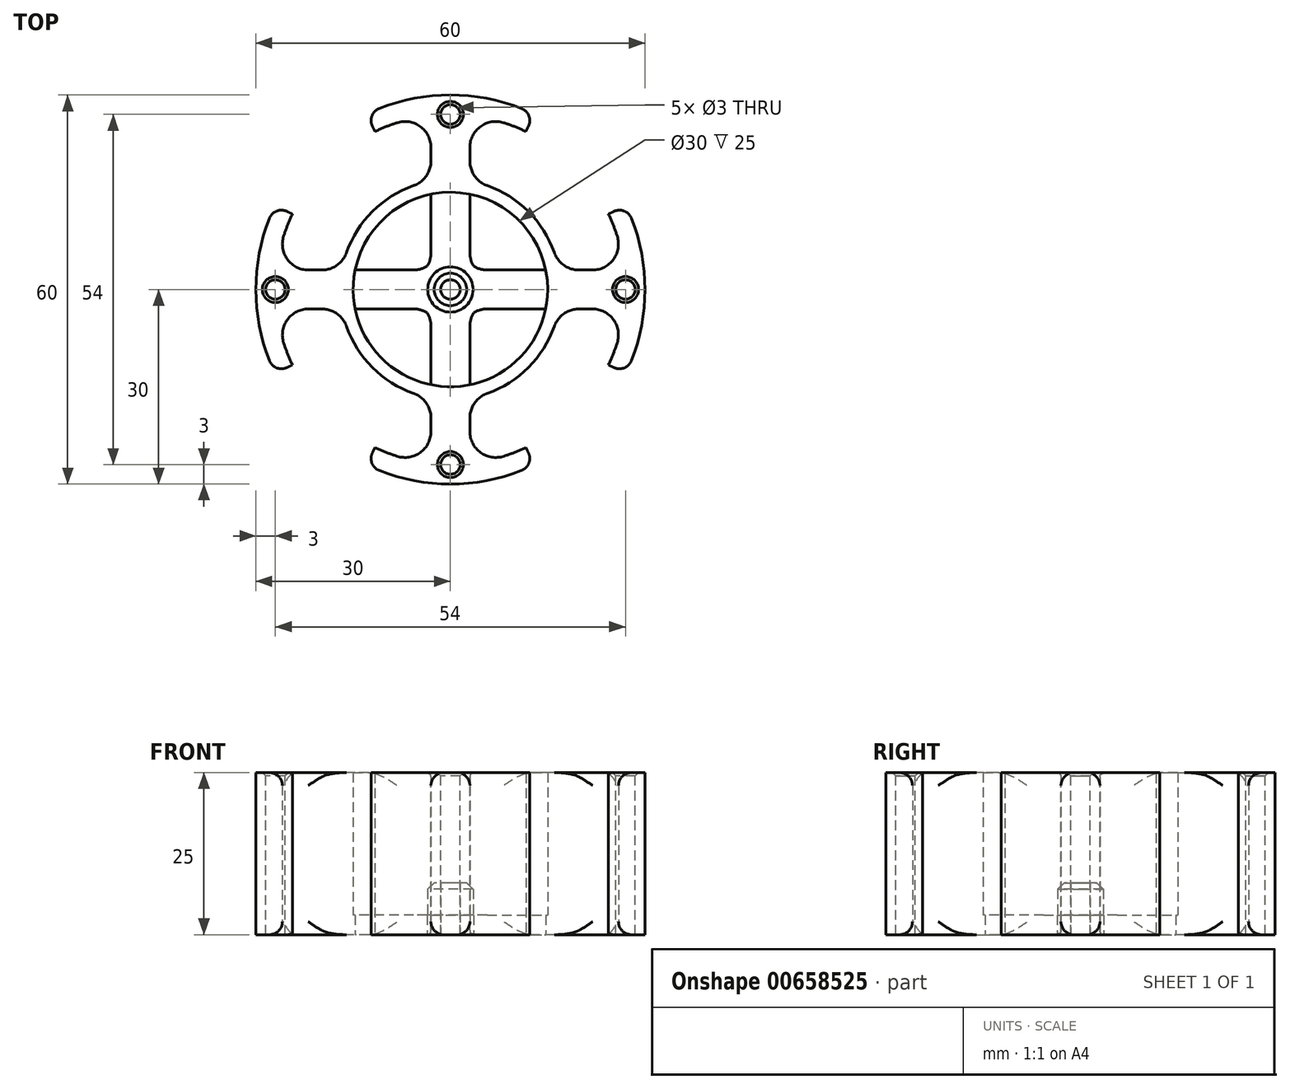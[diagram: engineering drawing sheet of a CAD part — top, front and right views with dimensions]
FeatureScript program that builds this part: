
annotation { "Feature Type Name" : "Feature", "Feature Type Description" : "" }
export const myFeature = defineFeature(function(context is Context, id is Id, definition is map)
    precondition{}
    {
        {
            var Q0;
            Q0=qCreatedBy(makeId("Top.planeOp"),FACE);
            var sketch = newSketch(context, id + "F0", { "sketchPlane" : qUnion([Q0])});
            skCircle(sketch, "E0", {"center": v(0, 0) * mm, "radius": 27 * mm});
            skCircle(sketch, "E1", {"center": v(0, 0) * mm, "radius": 15 * mm});
            skCircle(sketch, "E2", {"center": v(0, 0) * mm, "radius": 17 * mm});
            skCircle(sketch, "E3", {"center": v(0, 0) * mm, "radius": 30 * mm});
            skLineSegment(sketch, "E4", {"start": v(-3, 4) * mm, "end": v(-3, 26.83) * mm});
            skLineSegment(sketch, "E5", {"start": v(3, 4) * mm, "end": v(3, 26.83) * mm});
            skCircle(sketch, "E6", {"center": v(0, 0) * mm, "radius": 5 * mm});
            skLineSegment(sketch, "E7.1.0", {"start": v(4, 3) * mm, "end": v(26.83, 3) * mm});
            skLineSegment(sketch, "E7.1.1", {"start": v(4, -3) * mm, "end": v(26.83, -3) * mm});
            skLineSegment(sketch, "E7.2.0", {"start": v(3, -4) * mm, "end": v(3, -26.83) * mm});
            skLineSegment(sketch, "E7.2.1", {"start": v(-3, -4) * mm, "end": v(-3, -26.83) * mm});
            skLineSegment(sketch, "E7.3.0", {"start": v(-4, -3) * mm, "end": v(-26.83, -3) * mm});
            skLineSegment(sketch, "E7.3.1", {"start": v(-4, 3) * mm, "end": v(-26.83, 3) * mm});
            skLineSegment(sketch, "E7.anchor1", {"start": v(0, 0) * mm, "end": v(-3, 4) * mm, "construction": true});
            skLineSegment(sketch, "E7.anchor2", {"start": v(0, 0) * mm, "end": v(-4, -3) * mm, "construction": true});
            skCircle(sketch, "E8", {"center": v(0, 0) * mm, "radius": 3.5 * mm});
            skCircle(sketch, "E9", {"center": v(0, 0) * mm, "radius": 1.5 * mm});
            skLineSegment(sketch, "E10", {"start": v(-24.36, 11.64) * mm, "end": v(-27.07, 12.93) * mm});
            skLineSegment(sketch, "E11", {"start": v(-11.64, 24.36) * mm, "end": v(-12.93, 27.07) * mm});
            skLineSegment(sketch, "E12", {"start": v(0, 0) * mm, "end": v(-21.21, 21.21) * mm, "construction": true});
            skLineSegment(sketch, "E13.1.0", {"start": v(24.36, 11.64) * mm, "end": v(27.07, 12.93) * mm});
            skLineSegment(sketch, "E13.1.1", {"start": v(11.64, 24.36) * mm, "end": v(12.93, 27.07) * mm});
            skLineSegment(sketch, "E13.2.0", {"start": v(11.64, -24.36) * mm, "end": v(12.93, -27.07) * mm});
            skLineSegment(sketch, "E13.2.1", {"start": v(24.36, -11.64) * mm, "end": v(27.07, -12.93) * mm});
            skLineSegment(sketch, "E13.3.0", {"start": v(-24.36, -11.64) * mm, "end": v(-27.07, -12.93) * mm});
            skLineSegment(sketch, "E13.3.1", {"start": v(-11.64, -24.36) * mm, "end": v(-12.93, -27.07) * mm});
            skLineSegment(sketch, "E13.anchor1", {"start": v(0, 0) * mm, "end": v(-11.64, 24.36) * mm, "construction": true});
            skLineSegment(sketch, "E13.anchor2", {"start": v(0, 0) * mm, "end": v(-24.36, -11.64) * mm, "construction": true});
            skSolve(sketch);
        }
        {
            var Q0;
            Q0=makeQuery(id+"F0.imprint","IMPRINT",FACE,{"disambiguationData":[TD([[makeQuery(id+"F0.imprint","IMPRINT",EDGE,{"derivedFrom":sQuery(id+"F0.wireOp",EDGE,"E8")}),-1.0]])]});
            var Q1;
            {var subQ0=sQuery(id+"F0.wireOp",EDGE,"E7.3.1");var subQ1=sQuery(id+"F0.wireOp",EDGE,"E1");var subQ2=makeQuery(id+"F0.imprint","INTERSECT",VERTEX,{"derivedFrom":[subQ1,subQ0]});Q1=makeQuery(id+"F0.imprint","IMPRINT",FACE,{"disambiguationData":[TD([[makeQuery(id+"F0.imprint","IMPRINT",EDGE,{"disambiguationData":[TD([[subQ2,-1.0]])],"derivedFrom":subQ1}),1.0]])]});}
            var Q2;
            {var subQ0=sQuery(id+"F0.wireOp",EDGE,"E7.1.0");var subQ1=sQuery(id+"F0.wireOp",EDGE,"E1");var subQ2=makeQuery(id+"F0.imprint","INTERSECT",VERTEX,{"derivedFrom":[subQ1,subQ0]});Q2=makeQuery(id+"F0.imprint","IMPRINT",FACE,{"disambiguationData":[TD([[makeQuery(id+"F0.imprint","IMPRINT",EDGE,{"disambiguationData":[TD([[subQ2,1.0]])],"derivedFrom":subQ1}),1.0]])]});}
            var Q3;
            {var subQ0=sQuery(id+"F0.wireOp",EDGE,"E5");var subQ1=sQuery(id+"F0.wireOp",EDGE,"E1");var subQ2=makeQuery(id+"F0.imprint","INTERSECT",VERTEX,{"derivedFrom":[subQ1,subQ0]});Q3=makeQuery(id+"F0.imprint","IMPRINT",FACE,{"disambiguationData":[TD([[makeQuery(id+"F0.imprint","IMPRINT",EDGE,{"disambiguationData":[TD([[subQ2,-1.0]])],"derivedFrom":subQ1}),1.0]])]});}
            var Q4;
            {var subQ0=sQuery(id+"F0.wireOp",EDGE,"E7.2.1");var subQ1=sQuery(id+"F0.wireOp",EDGE,"E1");var subQ2=makeQuery(id+"F0.imprint","INTERSECT",VERTEX,{"derivedFrom":[subQ1,subQ0]});Q4=makeQuery(id+"F0.imprint","IMPRINT",FACE,{"disambiguationData":[TD([[makeQuery(id+"F0.imprint","IMPRINT",EDGE,{"disambiguationData":[TD([[subQ2,-1.0]])],"derivedFrom":subQ1}),1.0]])]});}
            extrude(context, id + "F1", {"entities" : qUnion([Q0, Q1, Q2, Q3, Q4]), "depth" : 3 * mm, "offsetDistance" : 25 * mm});
        }
        {
            var Q0;
            {var subQ0=sQuery(id+"F0.wireOp",EDGE,"E13.1.0");Q0=makeQuery(id+"F0.imprint","IMPRINT",FACE,{"disambiguationData":[TD([[makeQuery(id+"F0.imprint","IMPRINT",EDGE,{"derivedFrom":subQ0}),-1.0]])]});}
            var Q1;
            {var subQ2=sQuery(id+"F0.wireOp",EDGE,"E11");Q1=makeQuery(id+"F0.imprint","IMPRINT",FACE,{"disambiguationData":[TD([[makeQuery(id+"F0.imprint","IMPRINT",EDGE,{"derivedFrom":subQ2}),-1.0]])]});}
            var Q2;
            {var subQ0=sQuery(id+"F0.wireOp",EDGE,"E10");Q2=makeQuery(id+"F0.imprint","IMPRINT",FACE,{"disambiguationData":[TD([[makeQuery(id+"F0.imprint","IMPRINT",EDGE,{"derivedFrom":subQ0}),1.0]])]});}
            var Q3;
            {var subQ0=sQuery(id+"F0.wireOp",EDGE,"E13.2.0");Q3=makeQuery(id+"F0.imprint","IMPRINT",FACE,{"disambiguationData":[TD([[makeQuery(id+"F0.imprint","IMPRINT",EDGE,{"derivedFrom":subQ0}),-1.0]])]});}
            var Q4;
            {var subQ0=sQuery(id+"F0.wireOp",EDGE,"E7.3.0");var subQ1=sQuery(id+"F0.wireOp",EDGE,"E0");var subQ2=makeQuery(id+"F0.imprint","INTERSECT",VERTEX,{"derivedFrom":[subQ1,subQ0]});Q4=makeQuery(id+"F0.imprint","IMPRINT",FACE,{"disambiguationData":[TD([[makeQuery(id+"F0.imprint","IMPRINT",EDGE,{"disambiguationData":[TD([[subQ2,1.0]])],"derivedFrom":subQ1}),1.0]])]});}
            var Q5;
            {var subQ0=sQuery(id+"F0.wireOp",EDGE,"E7.3.1");var subQ1=sQuery(id+"F0.wireOp",EDGE,"E1");var subQ2=makeQuery(id+"F0.imprint","INTERSECT",VERTEX,{"derivedFrom":[subQ1,subQ0]});Q5=makeQuery(id+"F0.imprint","IMPRINT",FACE,{"disambiguationData":[TD([[makeQuery(id+"F0.imprint","IMPRINT",EDGE,{"disambiguationData":[TD([[subQ2,-1.0]])],"derivedFrom":subQ1}),-1.0]])]});}
            var Q6;
            {var subQ0=sQuery(id+"F0.wireOp",EDGE,"E7.1.0");var subQ1=sQuery(id+"F0.wireOp",EDGE,"E1");var subQ2=makeQuery(id+"F0.imprint","INTERSECT",VERTEX,{"derivedFrom":[subQ1,subQ0]});Q6=makeQuery(id+"F0.imprint","IMPRINT",FACE,{"disambiguationData":[TD([[makeQuery(id+"F0.imprint","IMPRINT",EDGE,{"disambiguationData":[TD([[subQ2,1.0]])],"derivedFrom":subQ1}),-1.0]])]});}
            var Q7;
            {var subQ0=sQuery(id+"F0.wireOp",EDGE,"E7.1.0");var subQ1=sQuery(id+"F0.wireOp",EDGE,"E0");var subQ2=makeQuery(id+"F0.imprint","INTERSECT",VERTEX,{"derivedFrom":[subQ1,subQ0]});Q7=makeQuery(id+"F0.imprint","IMPRINT",FACE,{"disambiguationData":[TD([[makeQuery(id+"F0.imprint","IMPRINT",EDGE,{"disambiguationData":[TD([[subQ2,1.0]])],"derivedFrom":subQ1}),1.0]])]});}
            var Q8;
            {var subQ0=sQuery(id+"F0.wireOp",EDGE,"E5");var subQ1=sQuery(id+"F0.wireOp",EDGE,"E1");var subQ2=makeQuery(id+"F0.imprint","INTERSECT",VERTEX,{"derivedFrom":[subQ1,subQ0]});Q8=makeQuery(id+"F0.imprint","IMPRINT",FACE,{"disambiguationData":[TD([[makeQuery(id+"F0.imprint","IMPRINT",EDGE,{"disambiguationData":[TD([[subQ2,-1.0]])],"derivedFrom":subQ1}),-1.0]])]});}
            var Q9;
            {var subQ0=sQuery(id+"F0.wireOp",EDGE,"E4");var subQ1=sQuery(id+"F0.wireOp",EDGE,"E0");var subQ2=makeQuery(id+"F0.imprint","INTERSECT",VERTEX,{"derivedFrom":[subQ1,subQ0]});Q9=makeQuery(id+"F0.imprint","IMPRINT",FACE,{"disambiguationData":[TD([[makeQuery(id+"F0.imprint","IMPRINT",EDGE,{"disambiguationData":[TD([[subQ2,1.0]])],"derivedFrom":subQ1}),1.0]])]});}
            var Q10;
            {var subQ0=sQuery(id+"F0.wireOp",EDGE,"E5");var subQ1=sQuery(id+"F0.wireOp",EDGE,"E1");var subQ2=makeQuery(id+"F0.imprint","INTERSECT",VERTEX,{"derivedFrom":[subQ1,subQ0]});Q10=makeQuery(id+"F0.imprint","IMPRINT",FACE,{"disambiguationData":[TD([[makeQuery(id+"F0.imprint","IMPRINT",EDGE,{"disambiguationData":[TD([[subQ2,1.0]])],"derivedFrom":subQ1}),-1.0]])]});}
            var Q11;
            {var subQ0=sQuery(id+"F0.wireOp",EDGE,"E4");var subQ1=sQuery(id+"F0.wireOp",EDGE,"E1");var subQ2=makeQuery(id+"F0.imprint","INTERSECT",VERTEX,{"derivedFrom":[subQ1,subQ0]});Q11=makeQuery(id+"F0.imprint","IMPRINT",FACE,{"disambiguationData":[TD([[makeQuery(id+"F0.imprint","IMPRINT",EDGE,{"disambiguationData":[TD([[subQ2,-1.0]])],"derivedFrom":subQ1}),-1.0]])]});}
            var Q12;
            {var subQ0=sQuery(id+"F0.wireOp",EDGE,"E7.2.0");var subQ1=sQuery(id+"F0.wireOp",EDGE,"E0");var subQ2=makeQuery(id+"F0.imprint","INTERSECT",VERTEX,{"derivedFrom":[subQ1,subQ0]});Q12=makeQuery(id+"F0.imprint","IMPRINT",FACE,{"disambiguationData":[TD([[makeQuery(id+"F0.imprint","IMPRINT",EDGE,{"disambiguationData":[TD([[subQ2,1.0]])],"derivedFrom":subQ1}),1.0]])]});}
            var Q13;
            {var subQ0=sQuery(id+"F0.wireOp",EDGE,"E7.2.1");var subQ1=sQuery(id+"F0.wireOp",EDGE,"E1");var subQ2=makeQuery(id+"F0.imprint","INTERSECT",VERTEX,{"derivedFrom":[subQ1,subQ0]});Q13=makeQuery(id+"F0.imprint","IMPRINT",FACE,{"disambiguationData":[TD([[makeQuery(id+"F0.imprint","IMPRINT",EDGE,{"disambiguationData":[TD([[subQ2,-1.0]])],"derivedFrom":subQ1}),-1.0]])]});}
            var Q14;
            {var subQ0=sQuery(id+"F0.wireOp",EDGE,"E7.3.0");var subQ1=sQuery(id+"F0.wireOp",EDGE,"E1");var subQ2=makeQuery(id+"F0.imprint","INTERSECT",VERTEX,{"derivedFrom":[subQ1,subQ0]});Q14=makeQuery(id+"F0.imprint","IMPRINT",FACE,{"disambiguationData":[TD([[makeQuery(id+"F0.imprint","IMPRINT",EDGE,{"disambiguationData":[TD([[subQ2,-1.0]])],"derivedFrom":subQ1}),-1.0]])]});}
            var Q15;
            {var subQ0=sQuery(id+"F0.wireOp",EDGE,"E7.2.0");var subQ1=sQuery(id+"F0.wireOp",EDGE,"E1");var subQ2=makeQuery(id+"F0.imprint","INTERSECT",VERTEX,{"derivedFrom":[subQ1,subQ0]});Q15=makeQuery(id+"F0.imprint","IMPRINT",FACE,{"disambiguationData":[TD([[makeQuery(id+"F0.imprint","IMPRINT",EDGE,{"disambiguationData":[TD([[subQ2,-1.0]])],"derivedFrom":subQ1}),-1.0]])]});}
            extrude(context, id + "F2", {"entities" : qUnion([Q0, Q1, Q2, Q3, Q4, Q5, Q6, Q7, Q8, Q9, Q10, Q11, Q12, Q13, Q14, Q15]), "operationType" : NewBodyOperationType.ADD, "depth" : 25 * mm, "offsetDistance" : 25 * mm});
        }
        {
            var Q0;
            Q0=makeQuery(id+"F0.imprint","IMPRINT",FACE,{"disambiguationData":[TD([[makeQuery(id+"F0.imprint","IMPRINT",EDGE,{"derivedFrom":sQuery(id+"F0.wireOp",EDGE,"E8")}),1.0]])]});
            extrude(context, id + "F3", {"entities" : qUnion([Q0]), "operationType" : NewBodyOperationType.ADD, "depth" : 8 * mm, "offsetDistance" : 25 * mm});
        }
        {
            var Q0;
            Q0=makeQuery(id+"F3.opExtrude","CAP_EDGE",EDGE,{"disambiguationData":[OSD([sQuery(id+"F0.wireOp",EDGE,"E8")])],"isStart":false});
            chamfer(context, id + "F4", {"entities" : qUnion([Q0]), "width" : 1 * mm, "tangentPropagation" : true});
        }
        {
            var Q0;
            Q0=makeQuery(id+"F2.opExtrude","SWEPT_EDGE",EDGE,{"disambiguationData":[OSD([sQuery(id+"F0.wireOp",EDGE,"E0"),sQuery(id+"F0.wireOp",EDGE,"E7.1.0")])]});
            var Q1;
            Q1=makeQuery(id+"F2.opExtrude","SWEPT_EDGE",EDGE,{"disambiguationData":[OSD([sQuery(id+"F0.wireOp",EDGE,"E2"),sQuery(id+"F0.wireOp",EDGE,"E7.1.0")])]});
            var Q2;
            Q2=makeQuery(id+"F2.opExtrude","SWEPT_EDGE",EDGE,{"disambiguationData":[OSD([sQuery(id+"F0.wireOp",EDGE,"E2"),sQuery(id+"F0.wireOp",EDGE,"E5")])]});
            var Q3;
            Q3=makeQuery(id+"F2.opExtrude","SWEPT_EDGE",EDGE,{"disambiguationData":[OSD([sQuery(id+"F0.wireOp",EDGE,"E0"),sQuery(id+"F0.wireOp",EDGE,"E5")])]});
            var Q4;
            Q4=makeQuery(id+"F2.opExtrude","SWEPT_EDGE",EDGE,{"disambiguationData":[OSD([sQuery(id+"F0.wireOp",EDGE,"E2"),sQuery(id+"F0.wireOp",EDGE,"E4")])]});
            var Q5;
            Q5=makeQuery(id+"F2.opExtrude","SWEPT_EDGE",EDGE,{"disambiguationData":[OSD([sQuery(id+"F0.wireOp",EDGE,"E0"),sQuery(id+"F0.wireOp",EDGE,"E4")])]});
            var Q6;
            Q6=makeQuery(id+"F2.opExtrude","SWEPT_EDGE",EDGE,{"disambiguationData":[OSD([sQuery(id+"F0.wireOp",EDGE,"E2"),sQuery(id+"F0.wireOp",EDGE,"E7.3.1")])]});
            var Q7;
            Q7=makeQuery(id+"F2.opExtrude","SWEPT_EDGE",EDGE,{"disambiguationData":[OSD([sQuery(id+"F0.wireOp",EDGE,"E0"),sQuery(id+"F0.wireOp",EDGE,"E7.3.1")])]});
            var Q8;
            Q8=makeQuery(id+"F2.opExtrude","SWEPT_EDGE",EDGE,{"disambiguationData":[OSD([sQuery(id+"F0.wireOp",EDGE,"E0"),sQuery(id+"F0.wireOp",EDGE,"E7.2.0")])]});
            var Q9;
            Q9=makeQuery(id+"F2.opExtrude","SWEPT_EDGE",EDGE,{"disambiguationData":[OSD([sQuery(id+"F0.wireOp",EDGE,"E2"),sQuery(id+"F0.wireOp",EDGE,"E7.2.0")])]});
            var Q10;
            Q10=makeQuery(id+"F2.opExtrude","SWEPT_EDGE",EDGE,{"disambiguationData":[OSD([sQuery(id+"F0.wireOp",EDGE,"E2"),sQuery(id+"F0.wireOp",EDGE,"E7.1.1")])]});
            var Q11;
            Q11=makeQuery(id+"F2.opExtrude","SWEPT_EDGE",EDGE,{"disambiguationData":[OSD([sQuery(id+"F0.wireOp",EDGE,"E0"),sQuery(id+"F0.wireOp",EDGE,"E7.1.1")])]});
            var Q12;
            Q12=makeQuery(id+"F2.opExtrude","SWEPT_EDGE",EDGE,{"disambiguationData":[OSD([sQuery(id+"F0.wireOp",EDGE,"E0"),sQuery(id+"F0.wireOp",EDGE,"E7.3.0")])]});
            var Q13;
            Q13=makeQuery(id+"F2.opExtrude","SWEPT_EDGE",EDGE,{"disambiguationData":[OSD([sQuery(id+"F0.wireOp",EDGE,"E2"),sQuery(id+"F0.wireOp",EDGE,"E7.3.0")])]});
            var Q14;
            Q14=makeQuery(id+"F2.opExtrude","SWEPT_EDGE",EDGE,{"disambiguationData":[OSD([sQuery(id+"F0.wireOp",EDGE,"E2"),sQuery(id+"F0.wireOp",EDGE,"E7.2.1")])]});
            var Q15;
            Q15=makeQuery(id+"F2.opExtrude","SWEPT_EDGE",EDGE,{"disambiguationData":[OSD([sQuery(id+"F0.wireOp",EDGE,"E0"),sQuery(id+"F0.wireOp",EDGE,"E7.2.1")])]});
            var Q16;
            Q16=makeQuery(id+"F1.opExtrude","SWEPT_EDGE",EDGE,{"disambiguationData":[OSD([sQuery(id+"F0.wireOp",EDGE,"E1"),sQuery(id+"F0.wireOp",EDGE,"E7.3.0")])]});
            var Q17;
            Q17=makeQuery(id+"F1.opExtrude","SWEPT_EDGE",EDGE,{"disambiguationData":[OSD([sQuery(id+"F0.wireOp",EDGE,"E1"),sQuery(id+"F0.wireOp",EDGE,"E7.2.1")])]});
            var Q18;
            Q18=makeQuery(id+"F1.opExtrude","SWEPT_EDGE",EDGE,{"disambiguationData":[OSD([sQuery(id+"F0.wireOp",EDGE,"E1"),sQuery(id+"F0.wireOp",EDGE,"E7.2.0")])]});
            var Q19;
            Q19=makeQuery(id+"F1.opExtrude","SWEPT_EDGE",EDGE,{"disambiguationData":[OSD([sQuery(id+"F0.wireOp",EDGE,"E1"),sQuery(id+"F0.wireOp",EDGE,"E7.1.1")])]});
            var Q20;
            Q20=makeQuery(id+"F1.opExtrude","SWEPT_EDGE",EDGE,{"disambiguationData":[OSD([sQuery(id+"F0.wireOp",EDGE,"E1"),sQuery(id+"F0.wireOp",EDGE,"E4")])]});
            var Q21;
            Q21=makeQuery(id+"F1.opExtrude","SWEPT_EDGE",EDGE,{"disambiguationData":[OSD([sQuery(id+"F0.wireOp",EDGE,"E1"),sQuery(id+"F0.wireOp",EDGE,"E7.1.0")])]});
            var Q22;
            Q22=makeQuery(id+"F1.opExtrude","SWEPT_EDGE",EDGE,{"disambiguationData":[OSD([sQuery(id+"F0.wireOp",EDGE,"E1"),sQuery(id+"F0.wireOp",EDGE,"E5")])]});
            var Q23;
            Q23=makeQuery(id+"F1.opExtrude","SWEPT_EDGE",EDGE,{"disambiguationData":[OSD([sQuery(id+"F0.wireOp",EDGE,"E1"),sQuery(id+"F0.wireOp",EDGE,"E7.3.1")])]});
            var Q24;
            Q24=makeQuery(id+"F1.opExtrude","SWEPT_EDGE",EDGE,{"disambiguationData":[OSD([sQuery(id+"F0.wireOp",EDGE,"E4"),sQuery(id+"F0.wireOp",EDGE,"E6")])]});
            var Q25;
            Q25=makeQuery(id+"F1.opExtrude","SWEPT_EDGE",EDGE,{"disambiguationData":[OSD([sQuery(id+"F0.wireOp",EDGE,"E6"),sQuery(id+"F0.wireOp",EDGE,"E7.3.1")])]});
            var Q26;
            Q26=makeQuery(id+"F1.opExtrude","SWEPT_EDGE",EDGE,{"disambiguationData":[OSD([sQuery(id+"F0.wireOp",EDGE,"E6"),sQuery(id+"F0.wireOp",EDGE,"E7.3.0")])]});
            var Q27;
            Q27=makeQuery(id+"F1.opExtrude","SWEPT_EDGE",EDGE,{"disambiguationData":[OSD([sQuery(id+"F0.wireOp",EDGE,"E6"),sQuery(id+"F0.wireOp",EDGE,"E7.2.1")])]});
            var Q28;
            Q28=makeQuery(id+"F1.opExtrude","SWEPT_EDGE",EDGE,{"disambiguationData":[OSD([sQuery(id+"F0.wireOp",EDGE,"E6"),sQuery(id+"F0.wireOp",EDGE,"E7.2.0")])]});
            var Q29;
            Q29=makeQuery(id+"F1.opExtrude","SWEPT_EDGE",EDGE,{"disambiguationData":[OSD([sQuery(id+"F0.wireOp",EDGE,"E6"),sQuery(id+"F0.wireOp",EDGE,"E7.1.1")])]});
            var Q30;
            Q30=makeQuery(id+"F1.opExtrude","SWEPT_EDGE",EDGE,{"disambiguationData":[OSD([sQuery(id+"F0.wireOp",EDGE,"E5"),sQuery(id+"F0.wireOp",EDGE,"E6")])]});
            var Q31;
            Q31=makeQuery(id+"F1.opExtrude","SWEPT_EDGE",EDGE,{"disambiguationData":[OSD([sQuery(id+"F0.wireOp",EDGE,"E6"),sQuery(id+"F0.wireOp",EDGE,"E7.1.0")])]});
            fillet(context, id + "F5", {"entities" : qUnion([Q0, Q1, Q2, Q3, Q4, Q5, Q6, Q7, Q8, Q9, Q10, Q11, Q12, Q13, Q14, Q15, Q16, Q17, Q18, Q19, Q20, Q21, Q22, Q23, Q24, Q25, Q26, Q27, Q28, Q29, Q30, Q31]), "radius" : 4 * mm, "tangentPropagation" : true, "allowEdgeOverflow" : false});
        }
        {
            var Q0;
            Q0=makeQuery(id+"F2.opExtrude","CAP_FACE",FACE,{"disambiguationData":[OSD([sQuery(id+"F0.wireOp",EDGE,"E0"),sQuery(id+"F0.wireOp",EDGE,"E1"),sQuery(id+"F0.wireOp",EDGE,"E2"),sQuery(id+"F0.wireOp",EDGE,"E3"),sQuery(id+"F0.wireOp",EDGE,"E4"),sQuery(id+"F0.wireOp",EDGE,"E5"),sQuery(id+"F0.wireOp",EDGE,"E7.1.0"),sQuery(id+"F0.wireOp",EDGE,"E7.1.1"),sQuery(id+"F0.wireOp",EDGE,"E7.2.0"),sQuery(id+"F0.wireOp",EDGE,"E7.2.1"),sQuery(id+"F0.wireOp",EDGE,"E7.3.0"),sQuery(id+"F0.wireOp",EDGE,"E7.3.1")])],"isStart":false});
            var sketch = newSketch(context, id + "F6", { "sketchPlane" : qUnion([Q0])});
            skCircle(sketch, "E14.0", {"center": v(0, 0) * mm, "radius": 27 * mm});
            skPoint(sketch, "E15", {"position": v(0, 27) * mm});
            skPoint(sketch, "E16", {"position": v(27, 0) * mm});
            skPoint(sketch, "E17", {"position": v(-27, 0) * mm});
            skPoint(sketch, "E18", {"position": v(0, -27) * mm});
            skSolve(sketch);
        }
        {
            var Q0;
            Q0=sQuery(id+"F6.wireOp",VERTEX,"E15");
            var Q1;
            Q1=sQuery(id+"F6.wireOp",VERTEX,"E16");
            var Q2;
            Q2=sQuery(id+"F6.wireOp",VERTEX,"E18");
            var Q3;
            Q3=sQuery(id+"F6.wireOp",VERTEX,"E17");
            var Q4;
            Q4=makeQuery(id+"F1.opExtrude","SWEPT_BODY",BODY,{"disambiguationData":[OSD([sQuery(id+"F0.wireOp",EDGE,"E1"),sQuery(id+"F0.wireOp",EDGE,"E4"),sQuery(id+"F0.wireOp",EDGE,"E5"),sQuery(id+"F0.wireOp",EDGE,"E6"),sQuery(id+"F0.wireOp",EDGE,"E7.1.0"),sQuery(id+"F0.wireOp",EDGE,"E7.1.1"),sQuery(id+"F0.wireOp",EDGE,"E7.2.0"),sQuery(id+"F0.wireOp",EDGE,"E7.2.1"),sQuery(id+"F0.wireOp",EDGE,"E7.3.0"),sQuery(id+"F0.wireOp",EDGE,"E7.3.1"),sQuery(id+"F0.wireOp",EDGE,"E8")])]});
            hole(context, id + "F7", {"style" : HoleStyle.C_SINK, "endStyle" : HoleEndStyle.THROUGH, "holeDiameter" : 3 * mm, "cSinkDiameter" : 4 * mm, "cSinkAngle" : 90 * degree, "majorDiameter" : 5 * mm, "isTappedThrough" : true, "tappedDepth" : 12 * mm, "tapClearance" : 3, "startFromSketch" : true, "locations" : qUnion([Q0, Q1, Q2, Q3]), "scope" : qUnion([Q4])});
        }
        {
            var Q0;
            {var subQ0=sQuery(id+"F0.wireOp",EDGE,"E7.3.0");var subQ1=sQuery(id+"F0.wireOp",EDGE,"E0");Q0=makeQuery(id+"F5.opFillet","BLEND_EDGE",EDGE,{"blendedFrom":[makeQuery(id+"F2.opExtrude","SWEPT_EDGE",EDGE,{"disambiguationData":[OSD([subQ1,subQ0])]}),makeQuery(id+"F2.opExtrude","CAP_FACE",FACE,{"disambiguationData":[OSD([subQ1,sQuery(id+"F0.wireOp",EDGE,"E1"),sQuery(id+"F0.wireOp",EDGE,"E2"),sQuery(id+"F0.wireOp",EDGE,"E3"),sQuery(id+"F0.wireOp",EDGE,"E4"),sQuery(id+"F0.wireOp",EDGE,"E5"),sQuery(id+"F0.wireOp",EDGE,"E7.1.0"),sQuery(id+"F0.wireOp",EDGE,"E7.1.1"),sQuery(id+"F0.wireOp",EDGE,"E7.2.0"),sQuery(id+"F0.wireOp",EDGE,"E7.2.1"),subQ0,sQuery(id+"F0.wireOp",EDGE,"E7.3.1"),sQuery(id+"F0.wireOp",EDGE,"E10"),sQuery(id+"F0.wireOp",EDGE,"E11"),sQuery(id+"F0.wireOp",EDGE,"E13.1.0"),sQuery(id+"F0.wireOp",EDGE,"E13.1.1"),sQuery(id+"F0.wireOp",EDGE,"E13.2.0"),sQuery(id+"F0.wireOp",EDGE,"E13.2.1"),sQuery(id+"F0.wireOp",EDGE,"E13.3.0"),sQuery(id+"F0.wireOp",EDGE,"E13.3.1")])],"isStart":false})],"blendedInto":[makeQuery(id+"F2.opExtrude","CAP_FACE",FACE,{"disambiguationData":[OSD([subQ1,sQuery(id+"F0.wireOp",EDGE,"E1"),sQuery(id+"F0.wireOp",EDGE,"E2"),sQuery(id+"F0.wireOp",EDGE,"E3"),sQuery(id+"F0.wireOp",EDGE,"E4"),sQuery(id+"F0.wireOp",EDGE,"E5"),sQuery(id+"F0.wireOp",EDGE,"E7.1.0"),sQuery(id+"F0.wireOp",EDGE,"E7.1.1"),sQuery(id+"F0.wireOp",EDGE,"E7.2.0"),sQuery(id+"F0.wireOp",EDGE,"E7.2.1"),subQ0,sQuery(id+"F0.wireOp",EDGE,"E7.3.1"),sQuery(id+"F0.wireOp",EDGE,"E10"),sQuery(id+"F0.wireOp",EDGE,"E11"),sQuery(id+"F0.wireOp",EDGE,"E13.1.0"),sQuery(id+"F0.wireOp",EDGE,"E13.1.1"),sQuery(id+"F0.wireOp",EDGE,"E13.2.0"),sQuery(id+"F0.wireOp",EDGE,"E13.2.1"),sQuery(id+"F0.wireOp",EDGE,"E13.3.0"),sQuery(id+"F0.wireOp",EDGE,"E13.3.1")])],"isStart":false})]});}
            var Q1;
            {var subQ0=sQuery(id+"F0.wireOp",EDGE,"E7.3.1");var subQ1=sQuery(id+"F0.wireOp",EDGE,"E0");Q1=makeQuery(id+"F5.opFillet","BLEND_EDGE",EDGE,{"blendedFrom":[makeQuery(id+"F2.opExtrude","SWEPT_EDGE",EDGE,{"disambiguationData":[OSD([subQ1,subQ0])]}),makeQuery(id+"F2.opExtrude","CAP_FACE",FACE,{"disambiguationData":[OSD([subQ1,sQuery(id+"F0.wireOp",EDGE,"E1"),sQuery(id+"F0.wireOp",EDGE,"E2"),sQuery(id+"F0.wireOp",EDGE,"E3"),sQuery(id+"F0.wireOp",EDGE,"E4"),sQuery(id+"F0.wireOp",EDGE,"E5"),sQuery(id+"F0.wireOp",EDGE,"E7.1.0"),sQuery(id+"F0.wireOp",EDGE,"E7.1.1"),sQuery(id+"F0.wireOp",EDGE,"E7.2.0"),sQuery(id+"F0.wireOp",EDGE,"E7.2.1"),sQuery(id+"F0.wireOp",EDGE,"E7.3.0"),subQ0,sQuery(id+"F0.wireOp",EDGE,"E10"),sQuery(id+"F0.wireOp",EDGE,"E11"),sQuery(id+"F0.wireOp",EDGE,"E13.1.0"),sQuery(id+"F0.wireOp",EDGE,"E13.1.1"),sQuery(id+"F0.wireOp",EDGE,"E13.2.0"),sQuery(id+"F0.wireOp",EDGE,"E13.2.1"),sQuery(id+"F0.wireOp",EDGE,"E13.3.0"),sQuery(id+"F0.wireOp",EDGE,"E13.3.1")])],"isStart":false})],"blendedInto":[makeQuery(id+"F2.opExtrude","CAP_FACE",FACE,{"disambiguationData":[OSD([subQ1,sQuery(id+"F0.wireOp",EDGE,"E1"),sQuery(id+"F0.wireOp",EDGE,"E2"),sQuery(id+"F0.wireOp",EDGE,"E3"),sQuery(id+"F0.wireOp",EDGE,"E4"),sQuery(id+"F0.wireOp",EDGE,"E5"),sQuery(id+"F0.wireOp",EDGE,"E7.1.0"),sQuery(id+"F0.wireOp",EDGE,"E7.1.1"),sQuery(id+"F0.wireOp",EDGE,"E7.2.0"),sQuery(id+"F0.wireOp",EDGE,"E7.2.1"),sQuery(id+"F0.wireOp",EDGE,"E7.3.0"),subQ0,sQuery(id+"F0.wireOp",EDGE,"E10"),sQuery(id+"F0.wireOp",EDGE,"E11"),sQuery(id+"F0.wireOp",EDGE,"E13.1.0"),sQuery(id+"F0.wireOp",EDGE,"E13.1.1"),sQuery(id+"F0.wireOp",EDGE,"E13.2.0"),sQuery(id+"F0.wireOp",EDGE,"E13.2.1"),sQuery(id+"F0.wireOp",EDGE,"E13.3.0"),sQuery(id+"F0.wireOp",EDGE,"E13.3.1")])],"isStart":false})]});}
            var Q2;
            {var subQ0=sQuery(id+"F0.wireOp",EDGE,"E4");var subQ1=sQuery(id+"F0.wireOp",EDGE,"E0");Q2=makeQuery(id+"F5.opFillet","BLEND_EDGE",EDGE,{"blendedFrom":[makeQuery(id+"F2.opExtrude","SWEPT_EDGE",EDGE,{"disambiguationData":[OSD([subQ1,subQ0])]}),makeQuery(id+"F2.opExtrude","CAP_FACE",FACE,{"disambiguationData":[OSD([subQ1,sQuery(id+"F0.wireOp",EDGE,"E1"),sQuery(id+"F0.wireOp",EDGE,"E2"),sQuery(id+"F0.wireOp",EDGE,"E3"),subQ0,sQuery(id+"F0.wireOp",EDGE,"E5"),sQuery(id+"F0.wireOp",EDGE,"E7.1.0"),sQuery(id+"F0.wireOp",EDGE,"E7.1.1"),sQuery(id+"F0.wireOp",EDGE,"E7.2.0"),sQuery(id+"F0.wireOp",EDGE,"E7.2.1"),sQuery(id+"F0.wireOp",EDGE,"E7.3.0"),sQuery(id+"F0.wireOp",EDGE,"E7.3.1"),sQuery(id+"F0.wireOp",EDGE,"E10"),sQuery(id+"F0.wireOp",EDGE,"E11"),sQuery(id+"F0.wireOp",EDGE,"E13.1.0"),sQuery(id+"F0.wireOp",EDGE,"E13.1.1"),sQuery(id+"F0.wireOp",EDGE,"E13.2.0"),sQuery(id+"F0.wireOp",EDGE,"E13.2.1"),sQuery(id+"F0.wireOp",EDGE,"E13.3.0"),sQuery(id+"F0.wireOp",EDGE,"E13.3.1")])],"isStart":false})],"blendedInto":[makeQuery(id+"F2.opExtrude","CAP_FACE",FACE,{"disambiguationData":[OSD([subQ1,sQuery(id+"F0.wireOp",EDGE,"E1"),sQuery(id+"F0.wireOp",EDGE,"E2"),sQuery(id+"F0.wireOp",EDGE,"E3"),subQ0,sQuery(id+"F0.wireOp",EDGE,"E5"),sQuery(id+"F0.wireOp",EDGE,"E7.1.0"),sQuery(id+"F0.wireOp",EDGE,"E7.1.1"),sQuery(id+"F0.wireOp",EDGE,"E7.2.0"),sQuery(id+"F0.wireOp",EDGE,"E7.2.1"),sQuery(id+"F0.wireOp",EDGE,"E7.3.0"),sQuery(id+"F0.wireOp",EDGE,"E7.3.1"),sQuery(id+"F0.wireOp",EDGE,"E10"),sQuery(id+"F0.wireOp",EDGE,"E11"),sQuery(id+"F0.wireOp",EDGE,"E13.1.0"),sQuery(id+"F0.wireOp",EDGE,"E13.1.1"),sQuery(id+"F0.wireOp",EDGE,"E13.2.0"),sQuery(id+"F0.wireOp",EDGE,"E13.2.1"),sQuery(id+"F0.wireOp",EDGE,"E13.3.0"),sQuery(id+"F0.wireOp",EDGE,"E13.3.1")])],"isStart":false})]});}
            var Q3;
            {var subQ0=sQuery(id+"F0.wireOp",EDGE,"E7.2.1");var subQ1=sQuery(id+"F0.wireOp",EDGE,"E0");Q3=makeQuery(id+"F5.opFillet","BLEND_EDGE",EDGE,{"blendedFrom":[makeQuery(id+"F2.opExtrude","SWEPT_EDGE",EDGE,{"disambiguationData":[OSD([subQ1,subQ0])]}),makeQuery(id+"F2.opExtrude","CAP_FACE",FACE,{"disambiguationData":[OSD([subQ1,sQuery(id+"F0.wireOp",EDGE,"E1"),sQuery(id+"F0.wireOp",EDGE,"E2"),sQuery(id+"F0.wireOp",EDGE,"E3"),sQuery(id+"F0.wireOp",EDGE,"E4"),sQuery(id+"F0.wireOp",EDGE,"E5"),sQuery(id+"F0.wireOp",EDGE,"E7.1.0"),sQuery(id+"F0.wireOp",EDGE,"E7.1.1"),sQuery(id+"F0.wireOp",EDGE,"E7.2.0"),subQ0,sQuery(id+"F0.wireOp",EDGE,"E7.3.0"),sQuery(id+"F0.wireOp",EDGE,"E7.3.1"),sQuery(id+"F0.wireOp",EDGE,"E10"),sQuery(id+"F0.wireOp",EDGE,"E11"),sQuery(id+"F0.wireOp",EDGE,"E13.1.0"),sQuery(id+"F0.wireOp",EDGE,"E13.1.1"),sQuery(id+"F0.wireOp",EDGE,"E13.2.0"),sQuery(id+"F0.wireOp",EDGE,"E13.2.1"),sQuery(id+"F0.wireOp",EDGE,"E13.3.0"),sQuery(id+"F0.wireOp",EDGE,"E13.3.1")])],"isStart":false})],"blendedInto":[makeQuery(id+"F2.opExtrude","CAP_FACE",FACE,{"disambiguationData":[OSD([subQ1,sQuery(id+"F0.wireOp",EDGE,"E1"),sQuery(id+"F0.wireOp",EDGE,"E2"),sQuery(id+"F0.wireOp",EDGE,"E3"),sQuery(id+"F0.wireOp",EDGE,"E4"),sQuery(id+"F0.wireOp",EDGE,"E5"),sQuery(id+"F0.wireOp",EDGE,"E7.1.0"),sQuery(id+"F0.wireOp",EDGE,"E7.1.1"),sQuery(id+"F0.wireOp",EDGE,"E7.2.0"),subQ0,sQuery(id+"F0.wireOp",EDGE,"E7.3.0"),sQuery(id+"F0.wireOp",EDGE,"E7.3.1"),sQuery(id+"F0.wireOp",EDGE,"E10"),sQuery(id+"F0.wireOp",EDGE,"E11"),sQuery(id+"F0.wireOp",EDGE,"E13.1.0"),sQuery(id+"F0.wireOp",EDGE,"E13.1.1"),sQuery(id+"F0.wireOp",EDGE,"E13.2.0"),sQuery(id+"F0.wireOp",EDGE,"E13.2.1"),sQuery(id+"F0.wireOp",EDGE,"E13.3.0"),sQuery(id+"F0.wireOp",EDGE,"E13.3.1")])],"isStart":false})]});}
            var Q4;
            {var subQ0=sQuery(id+"F0.wireOp",EDGE,"E7.2.0");var subQ1=sQuery(id+"F0.wireOp",EDGE,"E0");Q4=makeQuery(id+"F5.opFillet","BLEND_EDGE",EDGE,{"blendedFrom":[makeQuery(id+"F2.opExtrude","SWEPT_EDGE",EDGE,{"disambiguationData":[OSD([subQ1,subQ0])]}),makeQuery(id+"F2.opExtrude","CAP_FACE",FACE,{"disambiguationData":[OSD([subQ1,sQuery(id+"F0.wireOp",EDGE,"E1"),sQuery(id+"F0.wireOp",EDGE,"E2"),sQuery(id+"F0.wireOp",EDGE,"E3"),sQuery(id+"F0.wireOp",EDGE,"E4"),sQuery(id+"F0.wireOp",EDGE,"E5"),sQuery(id+"F0.wireOp",EDGE,"E7.1.0"),sQuery(id+"F0.wireOp",EDGE,"E7.1.1"),subQ0,sQuery(id+"F0.wireOp",EDGE,"E7.2.1"),sQuery(id+"F0.wireOp",EDGE,"E7.3.0"),sQuery(id+"F0.wireOp",EDGE,"E7.3.1"),sQuery(id+"F0.wireOp",EDGE,"E10"),sQuery(id+"F0.wireOp",EDGE,"E11"),sQuery(id+"F0.wireOp",EDGE,"E13.1.0"),sQuery(id+"F0.wireOp",EDGE,"E13.1.1"),sQuery(id+"F0.wireOp",EDGE,"E13.2.0"),sQuery(id+"F0.wireOp",EDGE,"E13.2.1"),sQuery(id+"F0.wireOp",EDGE,"E13.3.0"),sQuery(id+"F0.wireOp",EDGE,"E13.3.1")])],"isStart":false})],"blendedInto":[makeQuery(id+"F2.opExtrude","CAP_FACE",FACE,{"disambiguationData":[OSD([subQ1,sQuery(id+"F0.wireOp",EDGE,"E1"),sQuery(id+"F0.wireOp",EDGE,"E2"),sQuery(id+"F0.wireOp",EDGE,"E3"),sQuery(id+"F0.wireOp",EDGE,"E4"),sQuery(id+"F0.wireOp",EDGE,"E5"),sQuery(id+"F0.wireOp",EDGE,"E7.1.0"),sQuery(id+"F0.wireOp",EDGE,"E7.1.1"),subQ0,sQuery(id+"F0.wireOp",EDGE,"E7.2.1"),sQuery(id+"F0.wireOp",EDGE,"E7.3.0"),sQuery(id+"F0.wireOp",EDGE,"E7.3.1"),sQuery(id+"F0.wireOp",EDGE,"E10"),sQuery(id+"F0.wireOp",EDGE,"E11"),sQuery(id+"F0.wireOp",EDGE,"E13.1.0"),sQuery(id+"F0.wireOp",EDGE,"E13.1.1"),sQuery(id+"F0.wireOp",EDGE,"E13.2.0"),sQuery(id+"F0.wireOp",EDGE,"E13.2.1"),sQuery(id+"F0.wireOp",EDGE,"E13.3.0"),sQuery(id+"F0.wireOp",EDGE,"E13.3.1")])],"isStart":false})]});}
            var Q5;
            {var subQ0=sQuery(id+"F0.wireOp",EDGE,"E7.1.1");var subQ1=sQuery(id+"F0.wireOp",EDGE,"E0");Q5=makeQuery(id+"F5.opFillet","BLEND_EDGE",EDGE,{"blendedFrom":[makeQuery(id+"F2.opExtrude","SWEPT_EDGE",EDGE,{"disambiguationData":[OSD([subQ1,subQ0])]}),makeQuery(id+"F2.opExtrude","CAP_FACE",FACE,{"disambiguationData":[OSD([subQ1,sQuery(id+"F0.wireOp",EDGE,"E1"),sQuery(id+"F0.wireOp",EDGE,"E2"),sQuery(id+"F0.wireOp",EDGE,"E3"),sQuery(id+"F0.wireOp",EDGE,"E4"),sQuery(id+"F0.wireOp",EDGE,"E5"),sQuery(id+"F0.wireOp",EDGE,"E7.1.0"),subQ0,sQuery(id+"F0.wireOp",EDGE,"E7.2.0"),sQuery(id+"F0.wireOp",EDGE,"E7.2.1"),sQuery(id+"F0.wireOp",EDGE,"E7.3.0"),sQuery(id+"F0.wireOp",EDGE,"E7.3.1"),sQuery(id+"F0.wireOp",EDGE,"E10"),sQuery(id+"F0.wireOp",EDGE,"E11"),sQuery(id+"F0.wireOp",EDGE,"E13.1.0"),sQuery(id+"F0.wireOp",EDGE,"E13.1.1"),sQuery(id+"F0.wireOp",EDGE,"E13.2.0"),sQuery(id+"F0.wireOp",EDGE,"E13.2.1"),sQuery(id+"F0.wireOp",EDGE,"E13.3.0"),sQuery(id+"F0.wireOp",EDGE,"E13.3.1")])],"isStart":false})],"blendedInto":[makeQuery(id+"F2.opExtrude","CAP_FACE",FACE,{"disambiguationData":[OSD([subQ1,sQuery(id+"F0.wireOp",EDGE,"E1"),sQuery(id+"F0.wireOp",EDGE,"E2"),sQuery(id+"F0.wireOp",EDGE,"E3"),sQuery(id+"F0.wireOp",EDGE,"E4"),sQuery(id+"F0.wireOp",EDGE,"E5"),sQuery(id+"F0.wireOp",EDGE,"E7.1.0"),subQ0,sQuery(id+"F0.wireOp",EDGE,"E7.2.0"),sQuery(id+"F0.wireOp",EDGE,"E7.2.1"),sQuery(id+"F0.wireOp",EDGE,"E7.3.0"),sQuery(id+"F0.wireOp",EDGE,"E7.3.1"),sQuery(id+"F0.wireOp",EDGE,"E10"),sQuery(id+"F0.wireOp",EDGE,"E11"),sQuery(id+"F0.wireOp",EDGE,"E13.1.0"),sQuery(id+"F0.wireOp",EDGE,"E13.1.1"),sQuery(id+"F0.wireOp",EDGE,"E13.2.0"),sQuery(id+"F0.wireOp",EDGE,"E13.2.1"),sQuery(id+"F0.wireOp",EDGE,"E13.3.0"),sQuery(id+"F0.wireOp",EDGE,"E13.3.1")])],"isStart":false})]});}
            var Q6;
            {var subQ0=sQuery(id+"F0.wireOp",EDGE,"E7.1.0");var subQ1=sQuery(id+"F0.wireOp",EDGE,"E0");Q6=makeQuery(id+"F5.opFillet","BLEND_EDGE",EDGE,{"blendedFrom":[makeQuery(id+"F2.opExtrude","SWEPT_EDGE",EDGE,{"disambiguationData":[OSD([subQ1,subQ0])]}),makeQuery(id+"F2.opExtrude","CAP_FACE",FACE,{"disambiguationData":[OSD([subQ1,sQuery(id+"F0.wireOp",EDGE,"E1"),sQuery(id+"F0.wireOp",EDGE,"E2"),sQuery(id+"F0.wireOp",EDGE,"E3"),sQuery(id+"F0.wireOp",EDGE,"E4"),sQuery(id+"F0.wireOp",EDGE,"E5"),subQ0,sQuery(id+"F0.wireOp",EDGE,"E7.1.1"),sQuery(id+"F0.wireOp",EDGE,"E7.2.0"),sQuery(id+"F0.wireOp",EDGE,"E7.2.1"),sQuery(id+"F0.wireOp",EDGE,"E7.3.0"),sQuery(id+"F0.wireOp",EDGE,"E7.3.1"),sQuery(id+"F0.wireOp",EDGE,"E10"),sQuery(id+"F0.wireOp",EDGE,"E11"),sQuery(id+"F0.wireOp",EDGE,"E13.1.0"),sQuery(id+"F0.wireOp",EDGE,"E13.1.1"),sQuery(id+"F0.wireOp",EDGE,"E13.2.0"),sQuery(id+"F0.wireOp",EDGE,"E13.2.1"),sQuery(id+"F0.wireOp",EDGE,"E13.3.0"),sQuery(id+"F0.wireOp",EDGE,"E13.3.1")])],"isStart":false})],"blendedInto":[makeQuery(id+"F2.opExtrude","CAP_FACE",FACE,{"disambiguationData":[OSD([subQ1,sQuery(id+"F0.wireOp",EDGE,"E1"),sQuery(id+"F0.wireOp",EDGE,"E2"),sQuery(id+"F0.wireOp",EDGE,"E3"),sQuery(id+"F0.wireOp",EDGE,"E4"),sQuery(id+"F0.wireOp",EDGE,"E5"),subQ0,sQuery(id+"F0.wireOp",EDGE,"E7.1.1"),sQuery(id+"F0.wireOp",EDGE,"E7.2.0"),sQuery(id+"F0.wireOp",EDGE,"E7.2.1"),sQuery(id+"F0.wireOp",EDGE,"E7.3.0"),sQuery(id+"F0.wireOp",EDGE,"E7.3.1"),sQuery(id+"F0.wireOp",EDGE,"E10"),sQuery(id+"F0.wireOp",EDGE,"E11"),sQuery(id+"F0.wireOp",EDGE,"E13.1.0"),sQuery(id+"F0.wireOp",EDGE,"E13.1.1"),sQuery(id+"F0.wireOp",EDGE,"E13.2.0"),sQuery(id+"F0.wireOp",EDGE,"E13.2.1"),sQuery(id+"F0.wireOp",EDGE,"E13.3.0"),sQuery(id+"F0.wireOp",EDGE,"E13.3.1")])],"isStart":false})]});}
            var Q7;
            {var subQ0=sQuery(id+"F0.wireOp",EDGE,"E5");var subQ1=sQuery(id+"F0.wireOp",EDGE,"E0");Q7=makeQuery(id+"F5.opFillet","BLEND_EDGE",EDGE,{"blendedFrom":[makeQuery(id+"F2.opExtrude","SWEPT_EDGE",EDGE,{"disambiguationData":[OSD([subQ1,subQ0])]}),makeQuery(id+"F2.opExtrude","CAP_FACE",FACE,{"disambiguationData":[OSD([subQ1,sQuery(id+"F0.wireOp",EDGE,"E1"),sQuery(id+"F0.wireOp",EDGE,"E2"),sQuery(id+"F0.wireOp",EDGE,"E3"),sQuery(id+"F0.wireOp",EDGE,"E4"),subQ0,sQuery(id+"F0.wireOp",EDGE,"E7.1.0"),sQuery(id+"F0.wireOp",EDGE,"E7.1.1"),sQuery(id+"F0.wireOp",EDGE,"E7.2.0"),sQuery(id+"F0.wireOp",EDGE,"E7.2.1"),sQuery(id+"F0.wireOp",EDGE,"E7.3.0"),sQuery(id+"F0.wireOp",EDGE,"E7.3.1"),sQuery(id+"F0.wireOp",EDGE,"E10"),sQuery(id+"F0.wireOp",EDGE,"E11"),sQuery(id+"F0.wireOp",EDGE,"E13.1.0"),sQuery(id+"F0.wireOp",EDGE,"E13.1.1"),sQuery(id+"F0.wireOp",EDGE,"E13.2.0"),sQuery(id+"F0.wireOp",EDGE,"E13.2.1"),sQuery(id+"F0.wireOp",EDGE,"E13.3.0"),sQuery(id+"F0.wireOp",EDGE,"E13.3.1")])],"isStart":false})],"blendedInto":[makeQuery(id+"F2.opExtrude","CAP_FACE",FACE,{"disambiguationData":[OSD([subQ1,sQuery(id+"F0.wireOp",EDGE,"E1"),sQuery(id+"F0.wireOp",EDGE,"E2"),sQuery(id+"F0.wireOp",EDGE,"E3"),sQuery(id+"F0.wireOp",EDGE,"E4"),subQ0,sQuery(id+"F0.wireOp",EDGE,"E7.1.0"),sQuery(id+"F0.wireOp",EDGE,"E7.1.1"),sQuery(id+"F0.wireOp",EDGE,"E7.2.0"),sQuery(id+"F0.wireOp",EDGE,"E7.2.1"),sQuery(id+"F0.wireOp",EDGE,"E7.3.0"),sQuery(id+"F0.wireOp",EDGE,"E7.3.1"),sQuery(id+"F0.wireOp",EDGE,"E10"),sQuery(id+"F0.wireOp",EDGE,"E11"),sQuery(id+"F0.wireOp",EDGE,"E13.1.0"),sQuery(id+"F0.wireOp",EDGE,"E13.1.1"),sQuery(id+"F0.wireOp",EDGE,"E13.2.0"),sQuery(id+"F0.wireOp",EDGE,"E13.2.1"),sQuery(id+"F0.wireOp",EDGE,"E13.3.0"),sQuery(id+"F0.wireOp",EDGE,"E13.3.1")])],"isStart":false})]});}
            var Q8;
            {var subQ0=sQuery(id+"F0.wireOp",EDGE,"E8");var subQ1=sQuery(id+"F0.wireOp",EDGE,"E7.3.1");var subQ2=sQuery(id+"F0.wireOp",EDGE,"E7.3.0");var subQ3=sQuery(id+"F0.wireOp",EDGE,"E7.2.1");var subQ4=sQuery(id+"F0.wireOp",EDGE,"E7.2.0");var subQ5=sQuery(id+"F0.wireOp",EDGE,"E7.1.1");var subQ6=sQuery(id+"F0.wireOp",EDGE,"E7.1.0");var subQ7=sQuery(id+"F0.wireOp",EDGE,"E5");var subQ8=sQuery(id+"F0.wireOp",EDGE,"E4");var subQ9=sQuery(id+"F0.wireOp",EDGE,"E1");var subQ10=sQuery(id+"F0.wireOp",EDGE,"E0");Q8=makeQuery(id+"F5.opFillet","BLEND_EDGE",EDGE,{"blendedFrom":[makeQuery(id+"F2.opExtrude","SWEPT_EDGE",EDGE,{"disambiguationData":[OSD([subQ10,subQ5])]}),makeQuery(id+"F3.boolean.opBoolean","MERGE",FACE,{"derivedFrom":[makeQuery(id+"F2.boolean.opBoolean","MERGE",FACE,{"derivedFrom":[makeQuery(id+"F1.opExtrude","CAP_FACE",FACE,{"disambiguationData":[OSD([subQ9,subQ8,subQ7,sQuery(id+"F0.wireOp",EDGE,"E6"),subQ6,subQ5,subQ4,subQ3,subQ2,subQ1,subQ0])],"isStart":true}),makeQuery(id+"F2.opExtrude","CAP_FACE",FACE,{"disambiguationData":[OSD([subQ10,subQ9,sQuery(id+"F0.wireOp",EDGE,"E2"),sQuery(id+"F0.wireOp",EDGE,"E3"),subQ8,subQ7,subQ6,subQ5,subQ4,subQ3,subQ2,subQ1,sQuery(id+"F0.wireOp",EDGE,"E10"),sQuery(id+"F0.wireOp",EDGE,"E11"),sQuery(id+"F0.wireOp",EDGE,"E13.1.0"),sQuery(id+"F0.wireOp",EDGE,"E13.1.1"),sQuery(id+"F0.wireOp",EDGE,"E13.2.0"),sQuery(id+"F0.wireOp",EDGE,"E13.2.1"),sQuery(id+"F0.wireOp",EDGE,"E13.3.0"),sQuery(id+"F0.wireOp",EDGE,"E13.3.1")])],"isStart":true})]}),makeQuery(id+"F3.opExtrude","CAP_FACE",FACE,{"disambiguationData":[OSD([subQ0,sQuery(id+"F0.wireOp",EDGE,"E9")])],"isStart":true})]})],"blendedInto":[makeQuery(id+"F3.boolean.opBoolean","MERGE",FACE,{"derivedFrom":[makeQuery(id+"F2.boolean.opBoolean","MERGE",FACE,{"derivedFrom":[makeQuery(id+"F1.opExtrude","CAP_FACE",FACE,{"disambiguationData":[OSD([subQ9,subQ8,subQ7,sQuery(id+"F0.wireOp",EDGE,"E6"),subQ6,subQ5,subQ4,subQ3,subQ2,subQ1,subQ0])],"isStart":true}),makeQuery(id+"F2.opExtrude","CAP_FACE",FACE,{"disambiguationData":[OSD([subQ10,subQ9,sQuery(id+"F0.wireOp",EDGE,"E2"),sQuery(id+"F0.wireOp",EDGE,"E3"),subQ8,subQ7,subQ6,subQ5,subQ4,subQ3,subQ2,subQ1,sQuery(id+"F0.wireOp",EDGE,"E10"),sQuery(id+"F0.wireOp",EDGE,"E11"),sQuery(id+"F0.wireOp",EDGE,"E13.1.0"),sQuery(id+"F0.wireOp",EDGE,"E13.1.1"),sQuery(id+"F0.wireOp",EDGE,"E13.2.0"),sQuery(id+"F0.wireOp",EDGE,"E13.2.1"),sQuery(id+"F0.wireOp",EDGE,"E13.3.0"),sQuery(id+"F0.wireOp",EDGE,"E13.3.1")])],"isStart":true})]}),makeQuery(id+"F3.opExtrude","CAP_FACE",FACE,{"disambiguationData":[OSD([subQ0,sQuery(id+"F0.wireOp",EDGE,"E9")])],"isStart":true})]})]});}
            var Q9;
            {var subQ0=sQuery(id+"F0.wireOp",EDGE,"E8");var subQ1=sQuery(id+"F0.wireOp",EDGE,"E7.3.1");var subQ2=sQuery(id+"F0.wireOp",EDGE,"E7.3.0");var subQ3=sQuery(id+"F0.wireOp",EDGE,"E7.2.1");var subQ4=sQuery(id+"F0.wireOp",EDGE,"E7.2.0");var subQ5=sQuery(id+"F0.wireOp",EDGE,"E7.1.1");var subQ6=sQuery(id+"F0.wireOp",EDGE,"E7.1.0");var subQ7=sQuery(id+"F0.wireOp",EDGE,"E5");var subQ8=sQuery(id+"F0.wireOp",EDGE,"E4");var subQ9=sQuery(id+"F0.wireOp",EDGE,"E1");var subQ10=sQuery(id+"F0.wireOp",EDGE,"E0");Q9=makeQuery(id+"F5.opFillet","BLEND_EDGE",EDGE,{"blendedFrom":[makeQuery(id+"F2.opExtrude","SWEPT_EDGE",EDGE,{"disambiguationData":[OSD([subQ10,subQ4])]}),makeQuery(id+"F3.boolean.opBoolean","MERGE",FACE,{"derivedFrom":[makeQuery(id+"F2.boolean.opBoolean","MERGE",FACE,{"derivedFrom":[makeQuery(id+"F1.opExtrude","CAP_FACE",FACE,{"disambiguationData":[OSD([subQ9,subQ8,subQ7,sQuery(id+"F0.wireOp",EDGE,"E6"),subQ6,subQ5,subQ4,subQ3,subQ2,subQ1,subQ0])],"isStart":true}),makeQuery(id+"F2.opExtrude","CAP_FACE",FACE,{"disambiguationData":[OSD([subQ10,subQ9,sQuery(id+"F0.wireOp",EDGE,"E2"),sQuery(id+"F0.wireOp",EDGE,"E3"),subQ8,subQ7,subQ6,subQ5,subQ4,subQ3,subQ2,subQ1,sQuery(id+"F0.wireOp",EDGE,"E10"),sQuery(id+"F0.wireOp",EDGE,"E11"),sQuery(id+"F0.wireOp",EDGE,"E13.1.0"),sQuery(id+"F0.wireOp",EDGE,"E13.1.1"),sQuery(id+"F0.wireOp",EDGE,"E13.2.0"),sQuery(id+"F0.wireOp",EDGE,"E13.2.1"),sQuery(id+"F0.wireOp",EDGE,"E13.3.0"),sQuery(id+"F0.wireOp",EDGE,"E13.3.1")])],"isStart":true})]}),makeQuery(id+"F3.opExtrude","CAP_FACE",FACE,{"disambiguationData":[OSD([subQ0,sQuery(id+"F0.wireOp",EDGE,"E9")])],"isStart":true})]})],"blendedInto":[makeQuery(id+"F3.boolean.opBoolean","MERGE",FACE,{"derivedFrom":[makeQuery(id+"F2.boolean.opBoolean","MERGE",FACE,{"derivedFrom":[makeQuery(id+"F1.opExtrude","CAP_FACE",FACE,{"disambiguationData":[OSD([subQ9,subQ8,subQ7,sQuery(id+"F0.wireOp",EDGE,"E6"),subQ6,subQ5,subQ4,subQ3,subQ2,subQ1,subQ0])],"isStart":true}),makeQuery(id+"F2.opExtrude","CAP_FACE",FACE,{"disambiguationData":[OSD([subQ10,subQ9,sQuery(id+"F0.wireOp",EDGE,"E2"),sQuery(id+"F0.wireOp",EDGE,"E3"),subQ8,subQ7,subQ6,subQ5,subQ4,subQ3,subQ2,subQ1,sQuery(id+"F0.wireOp",EDGE,"E10"),sQuery(id+"F0.wireOp",EDGE,"E11"),sQuery(id+"F0.wireOp",EDGE,"E13.1.0"),sQuery(id+"F0.wireOp",EDGE,"E13.1.1"),sQuery(id+"F0.wireOp",EDGE,"E13.2.0"),sQuery(id+"F0.wireOp",EDGE,"E13.2.1"),sQuery(id+"F0.wireOp",EDGE,"E13.3.0"),sQuery(id+"F0.wireOp",EDGE,"E13.3.1")])],"isStart":true})]}),makeQuery(id+"F3.opExtrude","CAP_FACE",FACE,{"disambiguationData":[OSD([subQ0,sQuery(id+"F0.wireOp",EDGE,"E9")])],"isStart":true})]})]});}
            var Q10;
            {var subQ0=sQuery(id+"F0.wireOp",EDGE,"E8");var subQ1=sQuery(id+"F0.wireOp",EDGE,"E7.3.1");var subQ2=sQuery(id+"F0.wireOp",EDGE,"E7.3.0");var subQ3=sQuery(id+"F0.wireOp",EDGE,"E7.2.1");var subQ4=sQuery(id+"F0.wireOp",EDGE,"E7.2.0");var subQ5=sQuery(id+"F0.wireOp",EDGE,"E7.1.1");var subQ6=sQuery(id+"F0.wireOp",EDGE,"E7.1.0");var subQ7=sQuery(id+"F0.wireOp",EDGE,"E5");var subQ8=sQuery(id+"F0.wireOp",EDGE,"E4");var subQ9=sQuery(id+"F0.wireOp",EDGE,"E1");var subQ10=sQuery(id+"F0.wireOp",EDGE,"E0");Q10=makeQuery(id+"F5.opFillet","BLEND_EDGE",EDGE,{"blendedFrom":[makeQuery(id+"F2.opExtrude","SWEPT_EDGE",EDGE,{"disambiguationData":[OSD([subQ10,subQ3])]}),makeQuery(id+"F3.boolean.opBoolean","MERGE",FACE,{"derivedFrom":[makeQuery(id+"F2.boolean.opBoolean","MERGE",FACE,{"derivedFrom":[makeQuery(id+"F1.opExtrude","CAP_FACE",FACE,{"disambiguationData":[OSD([subQ9,subQ8,subQ7,sQuery(id+"F0.wireOp",EDGE,"E6"),subQ6,subQ5,subQ4,subQ3,subQ2,subQ1,subQ0])],"isStart":true}),makeQuery(id+"F2.opExtrude","CAP_FACE",FACE,{"disambiguationData":[OSD([subQ10,subQ9,sQuery(id+"F0.wireOp",EDGE,"E2"),sQuery(id+"F0.wireOp",EDGE,"E3"),subQ8,subQ7,subQ6,subQ5,subQ4,subQ3,subQ2,subQ1,sQuery(id+"F0.wireOp",EDGE,"E10"),sQuery(id+"F0.wireOp",EDGE,"E11"),sQuery(id+"F0.wireOp",EDGE,"E13.1.0"),sQuery(id+"F0.wireOp",EDGE,"E13.1.1"),sQuery(id+"F0.wireOp",EDGE,"E13.2.0"),sQuery(id+"F0.wireOp",EDGE,"E13.2.1"),sQuery(id+"F0.wireOp",EDGE,"E13.3.0"),sQuery(id+"F0.wireOp",EDGE,"E13.3.1")])],"isStart":true})]}),makeQuery(id+"F3.opExtrude","CAP_FACE",FACE,{"disambiguationData":[OSD([subQ0,sQuery(id+"F0.wireOp",EDGE,"E9")])],"isStart":true})]})],"blendedInto":[makeQuery(id+"F3.boolean.opBoolean","MERGE",FACE,{"derivedFrom":[makeQuery(id+"F2.boolean.opBoolean","MERGE",FACE,{"derivedFrom":[makeQuery(id+"F1.opExtrude","CAP_FACE",FACE,{"disambiguationData":[OSD([subQ9,subQ8,subQ7,sQuery(id+"F0.wireOp",EDGE,"E6"),subQ6,subQ5,subQ4,subQ3,subQ2,subQ1,subQ0])],"isStart":true}),makeQuery(id+"F2.opExtrude","CAP_FACE",FACE,{"disambiguationData":[OSD([subQ10,subQ9,sQuery(id+"F0.wireOp",EDGE,"E2"),sQuery(id+"F0.wireOp",EDGE,"E3"),subQ8,subQ7,subQ6,subQ5,subQ4,subQ3,subQ2,subQ1,sQuery(id+"F0.wireOp",EDGE,"E10"),sQuery(id+"F0.wireOp",EDGE,"E11"),sQuery(id+"F0.wireOp",EDGE,"E13.1.0"),sQuery(id+"F0.wireOp",EDGE,"E13.1.1"),sQuery(id+"F0.wireOp",EDGE,"E13.2.0"),sQuery(id+"F0.wireOp",EDGE,"E13.2.1"),sQuery(id+"F0.wireOp",EDGE,"E13.3.0"),sQuery(id+"F0.wireOp",EDGE,"E13.3.1")])],"isStart":true})]}),makeQuery(id+"F3.opExtrude","CAP_FACE",FACE,{"disambiguationData":[OSD([subQ0,sQuery(id+"F0.wireOp",EDGE,"E9")])],"isStart":true})]})]});}
            var Q11;
            {var subQ0=sQuery(id+"F0.wireOp",EDGE,"E8");var subQ1=sQuery(id+"F0.wireOp",EDGE,"E7.3.1");var subQ2=sQuery(id+"F0.wireOp",EDGE,"E7.3.0");var subQ3=sQuery(id+"F0.wireOp",EDGE,"E7.2.1");var subQ4=sQuery(id+"F0.wireOp",EDGE,"E7.2.0");var subQ5=sQuery(id+"F0.wireOp",EDGE,"E7.1.1");var subQ6=sQuery(id+"F0.wireOp",EDGE,"E7.1.0");var subQ7=sQuery(id+"F0.wireOp",EDGE,"E5");var subQ8=sQuery(id+"F0.wireOp",EDGE,"E4");var subQ9=sQuery(id+"F0.wireOp",EDGE,"E1");var subQ10=sQuery(id+"F0.wireOp",EDGE,"E0");Q11=makeQuery(id+"F5.opFillet","BLEND_EDGE",EDGE,{"blendedFrom":[makeQuery(id+"F2.opExtrude","SWEPT_EDGE",EDGE,{"disambiguationData":[OSD([subQ10,subQ2])]}),makeQuery(id+"F3.boolean.opBoolean","MERGE",FACE,{"derivedFrom":[makeQuery(id+"F2.boolean.opBoolean","MERGE",FACE,{"derivedFrom":[makeQuery(id+"F1.opExtrude","CAP_FACE",FACE,{"disambiguationData":[OSD([subQ9,subQ8,subQ7,sQuery(id+"F0.wireOp",EDGE,"E6"),subQ6,subQ5,subQ4,subQ3,subQ2,subQ1,subQ0])],"isStart":true}),makeQuery(id+"F2.opExtrude","CAP_FACE",FACE,{"disambiguationData":[OSD([subQ10,subQ9,sQuery(id+"F0.wireOp",EDGE,"E2"),sQuery(id+"F0.wireOp",EDGE,"E3"),subQ8,subQ7,subQ6,subQ5,subQ4,subQ3,subQ2,subQ1,sQuery(id+"F0.wireOp",EDGE,"E10"),sQuery(id+"F0.wireOp",EDGE,"E11"),sQuery(id+"F0.wireOp",EDGE,"E13.1.0"),sQuery(id+"F0.wireOp",EDGE,"E13.1.1"),sQuery(id+"F0.wireOp",EDGE,"E13.2.0"),sQuery(id+"F0.wireOp",EDGE,"E13.2.1"),sQuery(id+"F0.wireOp",EDGE,"E13.3.0"),sQuery(id+"F0.wireOp",EDGE,"E13.3.1")])],"isStart":true})]}),makeQuery(id+"F3.opExtrude","CAP_FACE",FACE,{"disambiguationData":[OSD([subQ0,sQuery(id+"F0.wireOp",EDGE,"E9")])],"isStart":true})]})],"blendedInto":[makeQuery(id+"F3.boolean.opBoolean","MERGE",FACE,{"derivedFrom":[makeQuery(id+"F2.boolean.opBoolean","MERGE",FACE,{"derivedFrom":[makeQuery(id+"F1.opExtrude","CAP_FACE",FACE,{"disambiguationData":[OSD([subQ9,subQ8,subQ7,sQuery(id+"F0.wireOp",EDGE,"E6"),subQ6,subQ5,subQ4,subQ3,subQ2,subQ1,subQ0])],"isStart":true}),makeQuery(id+"F2.opExtrude","CAP_FACE",FACE,{"disambiguationData":[OSD([subQ10,subQ9,sQuery(id+"F0.wireOp",EDGE,"E2"),sQuery(id+"F0.wireOp",EDGE,"E3"),subQ8,subQ7,subQ6,subQ5,subQ4,subQ3,subQ2,subQ1,sQuery(id+"F0.wireOp",EDGE,"E10"),sQuery(id+"F0.wireOp",EDGE,"E11"),sQuery(id+"F0.wireOp",EDGE,"E13.1.0"),sQuery(id+"F0.wireOp",EDGE,"E13.1.1"),sQuery(id+"F0.wireOp",EDGE,"E13.2.0"),sQuery(id+"F0.wireOp",EDGE,"E13.2.1"),sQuery(id+"F0.wireOp",EDGE,"E13.3.0"),sQuery(id+"F0.wireOp",EDGE,"E13.3.1")])],"isStart":true})]}),makeQuery(id+"F3.opExtrude","CAP_FACE",FACE,{"disambiguationData":[OSD([subQ0,sQuery(id+"F0.wireOp",EDGE,"E9")])],"isStart":true})]})]});}
            var Q12;
            {var subQ0=sQuery(id+"F0.wireOp",EDGE,"E8");var subQ1=sQuery(id+"F0.wireOp",EDGE,"E7.3.1");var subQ2=sQuery(id+"F0.wireOp",EDGE,"E7.3.0");var subQ3=sQuery(id+"F0.wireOp",EDGE,"E7.2.1");var subQ4=sQuery(id+"F0.wireOp",EDGE,"E7.2.0");var subQ5=sQuery(id+"F0.wireOp",EDGE,"E7.1.1");var subQ6=sQuery(id+"F0.wireOp",EDGE,"E7.1.0");var subQ7=sQuery(id+"F0.wireOp",EDGE,"E5");var subQ8=sQuery(id+"F0.wireOp",EDGE,"E4");var subQ9=sQuery(id+"F0.wireOp",EDGE,"E1");var subQ10=sQuery(id+"F0.wireOp",EDGE,"E0");Q12=makeQuery(id+"F5.opFillet","BLEND_EDGE",EDGE,{"blendedFrom":[makeQuery(id+"F2.opExtrude","SWEPT_EDGE",EDGE,{"disambiguationData":[OSD([subQ10,subQ1])]}),makeQuery(id+"F3.boolean.opBoolean","MERGE",FACE,{"derivedFrom":[makeQuery(id+"F2.boolean.opBoolean","MERGE",FACE,{"derivedFrom":[makeQuery(id+"F1.opExtrude","CAP_FACE",FACE,{"disambiguationData":[OSD([subQ9,subQ8,subQ7,sQuery(id+"F0.wireOp",EDGE,"E6"),subQ6,subQ5,subQ4,subQ3,subQ2,subQ1,subQ0])],"isStart":true}),makeQuery(id+"F2.opExtrude","CAP_FACE",FACE,{"disambiguationData":[OSD([subQ10,subQ9,sQuery(id+"F0.wireOp",EDGE,"E2"),sQuery(id+"F0.wireOp",EDGE,"E3"),subQ8,subQ7,subQ6,subQ5,subQ4,subQ3,subQ2,subQ1,sQuery(id+"F0.wireOp",EDGE,"E10"),sQuery(id+"F0.wireOp",EDGE,"E11"),sQuery(id+"F0.wireOp",EDGE,"E13.1.0"),sQuery(id+"F0.wireOp",EDGE,"E13.1.1"),sQuery(id+"F0.wireOp",EDGE,"E13.2.0"),sQuery(id+"F0.wireOp",EDGE,"E13.2.1"),sQuery(id+"F0.wireOp",EDGE,"E13.3.0"),sQuery(id+"F0.wireOp",EDGE,"E13.3.1")])],"isStart":true})]}),makeQuery(id+"F3.opExtrude","CAP_FACE",FACE,{"disambiguationData":[OSD([subQ0,sQuery(id+"F0.wireOp",EDGE,"E9")])],"isStart":true})]})],"blendedInto":[makeQuery(id+"F3.boolean.opBoolean","MERGE",FACE,{"derivedFrom":[makeQuery(id+"F2.boolean.opBoolean","MERGE",FACE,{"derivedFrom":[makeQuery(id+"F1.opExtrude","CAP_FACE",FACE,{"disambiguationData":[OSD([subQ9,subQ8,subQ7,sQuery(id+"F0.wireOp",EDGE,"E6"),subQ6,subQ5,subQ4,subQ3,subQ2,subQ1,subQ0])],"isStart":true}),makeQuery(id+"F2.opExtrude","CAP_FACE",FACE,{"disambiguationData":[OSD([subQ10,subQ9,sQuery(id+"F0.wireOp",EDGE,"E2"),sQuery(id+"F0.wireOp",EDGE,"E3"),subQ8,subQ7,subQ6,subQ5,subQ4,subQ3,subQ2,subQ1,sQuery(id+"F0.wireOp",EDGE,"E10"),sQuery(id+"F0.wireOp",EDGE,"E11"),sQuery(id+"F0.wireOp",EDGE,"E13.1.0"),sQuery(id+"F0.wireOp",EDGE,"E13.1.1"),sQuery(id+"F0.wireOp",EDGE,"E13.2.0"),sQuery(id+"F0.wireOp",EDGE,"E13.2.1"),sQuery(id+"F0.wireOp",EDGE,"E13.3.0"),sQuery(id+"F0.wireOp",EDGE,"E13.3.1")])],"isStart":true})]}),makeQuery(id+"F3.opExtrude","CAP_FACE",FACE,{"disambiguationData":[OSD([subQ0,sQuery(id+"F0.wireOp",EDGE,"E9")])],"isStart":true})]})]});}
            var Q13;
            {var subQ0=sQuery(id+"F0.wireOp",EDGE,"E8");var subQ1=sQuery(id+"F0.wireOp",EDGE,"E7.3.1");var subQ2=sQuery(id+"F0.wireOp",EDGE,"E7.3.0");var subQ3=sQuery(id+"F0.wireOp",EDGE,"E7.2.1");var subQ4=sQuery(id+"F0.wireOp",EDGE,"E7.2.0");var subQ5=sQuery(id+"F0.wireOp",EDGE,"E7.1.1");var subQ6=sQuery(id+"F0.wireOp",EDGE,"E7.1.0");var subQ7=sQuery(id+"F0.wireOp",EDGE,"E5");var subQ8=sQuery(id+"F0.wireOp",EDGE,"E4");var subQ9=sQuery(id+"F0.wireOp",EDGE,"E1");var subQ10=sQuery(id+"F0.wireOp",EDGE,"E0");Q13=makeQuery(id+"F5.opFillet","BLEND_EDGE",EDGE,{"blendedFrom":[makeQuery(id+"F2.opExtrude","SWEPT_EDGE",EDGE,{"disambiguationData":[OSD([subQ10,subQ8])]}),makeQuery(id+"F3.boolean.opBoolean","MERGE",FACE,{"derivedFrom":[makeQuery(id+"F2.boolean.opBoolean","MERGE",FACE,{"derivedFrom":[makeQuery(id+"F1.opExtrude","CAP_FACE",FACE,{"disambiguationData":[OSD([subQ9,subQ8,subQ7,sQuery(id+"F0.wireOp",EDGE,"E6"),subQ6,subQ5,subQ4,subQ3,subQ2,subQ1,subQ0])],"isStart":true}),makeQuery(id+"F2.opExtrude","CAP_FACE",FACE,{"disambiguationData":[OSD([subQ10,subQ9,sQuery(id+"F0.wireOp",EDGE,"E2"),sQuery(id+"F0.wireOp",EDGE,"E3"),subQ8,subQ7,subQ6,subQ5,subQ4,subQ3,subQ2,subQ1,sQuery(id+"F0.wireOp",EDGE,"E10"),sQuery(id+"F0.wireOp",EDGE,"E11"),sQuery(id+"F0.wireOp",EDGE,"E13.1.0"),sQuery(id+"F0.wireOp",EDGE,"E13.1.1"),sQuery(id+"F0.wireOp",EDGE,"E13.2.0"),sQuery(id+"F0.wireOp",EDGE,"E13.2.1"),sQuery(id+"F0.wireOp",EDGE,"E13.3.0"),sQuery(id+"F0.wireOp",EDGE,"E13.3.1")])],"isStart":true})]}),makeQuery(id+"F3.opExtrude","CAP_FACE",FACE,{"disambiguationData":[OSD([subQ0,sQuery(id+"F0.wireOp",EDGE,"E9")])],"isStart":true})]})],"blendedInto":[makeQuery(id+"F3.boolean.opBoolean","MERGE",FACE,{"derivedFrom":[makeQuery(id+"F2.boolean.opBoolean","MERGE",FACE,{"derivedFrom":[makeQuery(id+"F1.opExtrude","CAP_FACE",FACE,{"disambiguationData":[OSD([subQ9,subQ8,subQ7,sQuery(id+"F0.wireOp",EDGE,"E6"),subQ6,subQ5,subQ4,subQ3,subQ2,subQ1,subQ0])],"isStart":true}),makeQuery(id+"F2.opExtrude","CAP_FACE",FACE,{"disambiguationData":[OSD([subQ10,subQ9,sQuery(id+"F0.wireOp",EDGE,"E2"),sQuery(id+"F0.wireOp",EDGE,"E3"),subQ8,subQ7,subQ6,subQ5,subQ4,subQ3,subQ2,subQ1,sQuery(id+"F0.wireOp",EDGE,"E10"),sQuery(id+"F0.wireOp",EDGE,"E11"),sQuery(id+"F0.wireOp",EDGE,"E13.1.0"),sQuery(id+"F0.wireOp",EDGE,"E13.1.1"),sQuery(id+"F0.wireOp",EDGE,"E13.2.0"),sQuery(id+"F0.wireOp",EDGE,"E13.2.1"),sQuery(id+"F0.wireOp",EDGE,"E13.3.0"),sQuery(id+"F0.wireOp",EDGE,"E13.3.1")])],"isStart":true})]}),makeQuery(id+"F3.opExtrude","CAP_FACE",FACE,{"disambiguationData":[OSD([subQ0,sQuery(id+"F0.wireOp",EDGE,"E9")])],"isStart":true})]})]});}
            var Q14;
            {var subQ0=sQuery(id+"F0.wireOp",EDGE,"E8");var subQ1=sQuery(id+"F0.wireOp",EDGE,"E7.3.1");var subQ2=sQuery(id+"F0.wireOp",EDGE,"E7.3.0");var subQ3=sQuery(id+"F0.wireOp",EDGE,"E7.2.1");var subQ4=sQuery(id+"F0.wireOp",EDGE,"E7.2.0");var subQ5=sQuery(id+"F0.wireOp",EDGE,"E7.1.1");var subQ6=sQuery(id+"F0.wireOp",EDGE,"E7.1.0");var subQ7=sQuery(id+"F0.wireOp",EDGE,"E5");var subQ8=sQuery(id+"F0.wireOp",EDGE,"E4");var subQ9=sQuery(id+"F0.wireOp",EDGE,"E1");var subQ10=sQuery(id+"F0.wireOp",EDGE,"E0");Q14=makeQuery(id+"F5.opFillet","BLEND_EDGE",EDGE,{"blendedFrom":[makeQuery(id+"F2.opExtrude","SWEPT_EDGE",EDGE,{"disambiguationData":[OSD([subQ10,subQ7])]}),makeQuery(id+"F3.boolean.opBoolean","MERGE",FACE,{"derivedFrom":[makeQuery(id+"F2.boolean.opBoolean","MERGE",FACE,{"derivedFrom":[makeQuery(id+"F1.opExtrude","CAP_FACE",FACE,{"disambiguationData":[OSD([subQ9,subQ8,subQ7,sQuery(id+"F0.wireOp",EDGE,"E6"),subQ6,subQ5,subQ4,subQ3,subQ2,subQ1,subQ0])],"isStart":true}),makeQuery(id+"F2.opExtrude","CAP_FACE",FACE,{"disambiguationData":[OSD([subQ10,subQ9,sQuery(id+"F0.wireOp",EDGE,"E2"),sQuery(id+"F0.wireOp",EDGE,"E3"),subQ8,subQ7,subQ6,subQ5,subQ4,subQ3,subQ2,subQ1,sQuery(id+"F0.wireOp",EDGE,"E10"),sQuery(id+"F0.wireOp",EDGE,"E11"),sQuery(id+"F0.wireOp",EDGE,"E13.1.0"),sQuery(id+"F0.wireOp",EDGE,"E13.1.1"),sQuery(id+"F0.wireOp",EDGE,"E13.2.0"),sQuery(id+"F0.wireOp",EDGE,"E13.2.1"),sQuery(id+"F0.wireOp",EDGE,"E13.3.0"),sQuery(id+"F0.wireOp",EDGE,"E13.3.1")])],"isStart":true})]}),makeQuery(id+"F3.opExtrude","CAP_FACE",FACE,{"disambiguationData":[OSD([subQ0,sQuery(id+"F0.wireOp",EDGE,"E9")])],"isStart":true})]})],"blendedInto":[makeQuery(id+"F3.boolean.opBoolean","MERGE",FACE,{"derivedFrom":[makeQuery(id+"F2.boolean.opBoolean","MERGE",FACE,{"derivedFrom":[makeQuery(id+"F1.opExtrude","CAP_FACE",FACE,{"disambiguationData":[OSD([subQ9,subQ8,subQ7,sQuery(id+"F0.wireOp",EDGE,"E6"),subQ6,subQ5,subQ4,subQ3,subQ2,subQ1,subQ0])],"isStart":true}),makeQuery(id+"F2.opExtrude","CAP_FACE",FACE,{"disambiguationData":[OSD([subQ10,subQ9,sQuery(id+"F0.wireOp",EDGE,"E2"),sQuery(id+"F0.wireOp",EDGE,"E3"),subQ8,subQ7,subQ6,subQ5,subQ4,subQ3,subQ2,subQ1,sQuery(id+"F0.wireOp",EDGE,"E10"),sQuery(id+"F0.wireOp",EDGE,"E11"),sQuery(id+"F0.wireOp",EDGE,"E13.1.0"),sQuery(id+"F0.wireOp",EDGE,"E13.1.1"),sQuery(id+"F0.wireOp",EDGE,"E13.2.0"),sQuery(id+"F0.wireOp",EDGE,"E13.2.1"),sQuery(id+"F0.wireOp",EDGE,"E13.3.0"),sQuery(id+"F0.wireOp",EDGE,"E13.3.1")])],"isStart":true})]}),makeQuery(id+"F3.opExtrude","CAP_FACE",FACE,{"disambiguationData":[OSD([subQ0,sQuery(id+"F0.wireOp",EDGE,"E9")])],"isStart":true})]})]});}
            var Q15;
            {var subQ0=sQuery(id+"F0.wireOp",EDGE,"E8");var subQ1=sQuery(id+"F0.wireOp",EDGE,"E7.3.1");var subQ2=sQuery(id+"F0.wireOp",EDGE,"E7.3.0");var subQ3=sQuery(id+"F0.wireOp",EDGE,"E7.2.1");var subQ4=sQuery(id+"F0.wireOp",EDGE,"E7.2.0");var subQ5=sQuery(id+"F0.wireOp",EDGE,"E7.1.1");var subQ6=sQuery(id+"F0.wireOp",EDGE,"E7.1.0");var subQ7=sQuery(id+"F0.wireOp",EDGE,"E5");var subQ8=sQuery(id+"F0.wireOp",EDGE,"E4");var subQ9=sQuery(id+"F0.wireOp",EDGE,"E1");var subQ10=sQuery(id+"F0.wireOp",EDGE,"E0");Q15=makeQuery(id+"F5.opFillet","BLEND_EDGE",EDGE,{"blendedFrom":[makeQuery(id+"F2.opExtrude","SWEPT_EDGE",EDGE,{"disambiguationData":[OSD([subQ10,subQ6])]}),makeQuery(id+"F3.boolean.opBoolean","MERGE",FACE,{"derivedFrom":[makeQuery(id+"F2.boolean.opBoolean","MERGE",FACE,{"derivedFrom":[makeQuery(id+"F1.opExtrude","CAP_FACE",FACE,{"disambiguationData":[OSD([subQ9,subQ8,subQ7,sQuery(id+"F0.wireOp",EDGE,"E6"),subQ6,subQ5,subQ4,subQ3,subQ2,subQ1,subQ0])],"isStart":true}),makeQuery(id+"F2.opExtrude","CAP_FACE",FACE,{"disambiguationData":[OSD([subQ10,subQ9,sQuery(id+"F0.wireOp",EDGE,"E2"),sQuery(id+"F0.wireOp",EDGE,"E3"),subQ8,subQ7,subQ6,subQ5,subQ4,subQ3,subQ2,subQ1,sQuery(id+"F0.wireOp",EDGE,"E10"),sQuery(id+"F0.wireOp",EDGE,"E11"),sQuery(id+"F0.wireOp",EDGE,"E13.1.0"),sQuery(id+"F0.wireOp",EDGE,"E13.1.1"),sQuery(id+"F0.wireOp",EDGE,"E13.2.0"),sQuery(id+"F0.wireOp",EDGE,"E13.2.1"),sQuery(id+"F0.wireOp",EDGE,"E13.3.0"),sQuery(id+"F0.wireOp",EDGE,"E13.3.1")])],"isStart":true})]}),makeQuery(id+"F3.opExtrude","CAP_FACE",FACE,{"disambiguationData":[OSD([subQ0,sQuery(id+"F0.wireOp",EDGE,"E9")])],"isStart":true})]})],"blendedInto":[makeQuery(id+"F3.boolean.opBoolean","MERGE",FACE,{"derivedFrom":[makeQuery(id+"F2.boolean.opBoolean","MERGE",FACE,{"derivedFrom":[makeQuery(id+"F1.opExtrude","CAP_FACE",FACE,{"disambiguationData":[OSD([subQ9,subQ8,subQ7,sQuery(id+"F0.wireOp",EDGE,"E6"),subQ6,subQ5,subQ4,subQ3,subQ2,subQ1,subQ0])],"isStart":true}),makeQuery(id+"F2.opExtrude","CAP_FACE",FACE,{"disambiguationData":[OSD([subQ10,subQ9,sQuery(id+"F0.wireOp",EDGE,"E2"),sQuery(id+"F0.wireOp",EDGE,"E3"),subQ8,subQ7,subQ6,subQ5,subQ4,subQ3,subQ2,subQ1,sQuery(id+"F0.wireOp",EDGE,"E10"),sQuery(id+"F0.wireOp",EDGE,"E11"),sQuery(id+"F0.wireOp",EDGE,"E13.1.0"),sQuery(id+"F0.wireOp",EDGE,"E13.1.1"),sQuery(id+"F0.wireOp",EDGE,"E13.2.0"),sQuery(id+"F0.wireOp",EDGE,"E13.2.1"),sQuery(id+"F0.wireOp",EDGE,"E13.3.0"),sQuery(id+"F0.wireOp",EDGE,"E13.3.1")])],"isStart":true})]}),makeQuery(id+"F3.opExtrude","CAP_FACE",FACE,{"disambiguationData":[OSD([subQ0,sQuery(id+"F0.wireOp",EDGE,"E9")])],"isStart":true})]})]});}
            var Q16;
            Q16=makeQuery(id+"F2.opExtrude","SWEPT_EDGE",EDGE,{"disambiguationData":[OSD([sQuery(id+"F0.wireOp",EDGE,"E3"),sQuery(id+"F0.wireOp",EDGE,"E13.2.0")])]});
            var Q17;
            Q17=makeQuery(id+"F2.opExtrude","SWEPT_EDGE",EDGE,{"disambiguationData":[OSD([sQuery(id+"F0.wireOp",EDGE,"E3"),sQuery(id+"F0.wireOp",EDGE,"E13.2.1")])]});
            var Q18;
            Q18=makeQuery(id+"F2.opExtrude","SWEPT_EDGE",EDGE,{"disambiguationData":[OSD([sQuery(id+"F0.wireOp",EDGE,"E3"),sQuery(id+"F0.wireOp",EDGE,"E13.3.1")])]});
            var Q19;
            Q19=makeQuery(id+"F2.opExtrude","SWEPT_EDGE",EDGE,{"disambiguationData":[OSD([sQuery(id+"F0.wireOp",EDGE,"E3"),sQuery(id+"F0.wireOp",EDGE,"E13.3.0")])]});
            var Q20;
            Q20=makeQuery(id+"F2.opExtrude","SWEPT_EDGE",EDGE,{"disambiguationData":[OSD([sQuery(id+"F0.wireOp",EDGE,"E3"),sQuery(id+"F0.wireOp",EDGE,"E11")])]});
            var Q21;
            Q21=makeQuery(id+"F2.opExtrude","SWEPT_EDGE",EDGE,{"disambiguationData":[OSD([sQuery(id+"F0.wireOp",EDGE,"E3"),sQuery(id+"F0.wireOp",EDGE,"E13.1.1")])]});
            var Q22;
            Q22=makeQuery(id+"F2.opExtrude","SWEPT_EDGE",EDGE,{"disambiguationData":[OSD([sQuery(id+"F0.wireOp",EDGE,"E3"),sQuery(id+"F0.wireOp",EDGE,"E13.1.0")])]});
            var Q23;
            Q23=makeQuery(id+"F2.opExtrude","SWEPT_EDGE",EDGE,{"disambiguationData":[OSD([sQuery(id+"F0.wireOp",EDGE,"E3"),sQuery(id+"F0.wireOp",EDGE,"E10")])]});
            fillet(context, id + "F8", {"entities" : qUnion([Q0, Q1, Q2, Q3, Q4, Q5, Q6, Q7, Q8, Q9, Q10, Q11, Q12, Q13, Q14, Q15, Q16, Q17, Q18, Q19, Q20, Q21, Q22, Q23]), "radius" : 2 * mm, "allowEdgeOverflow" : false});
        }
    });
